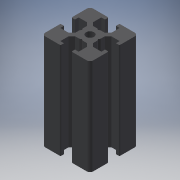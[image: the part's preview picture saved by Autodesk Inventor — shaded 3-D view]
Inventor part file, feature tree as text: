
AUTODESK INVENTOR PART (.ipt)
format: ipt  version: 2016 (Build 200138000, 138)  size: 172,544 bytes
history: native  units: mm
features: extrude x1, sketch x1
ambient origin geometry x8: Origin, YZ Plane, XZ Plane, XY Plane, X Axis, Y Axis, Z Axis, Center Point
bodies: Solid1 (feature_tree)
feature tree (2):
  extrude  "Extrusion1"  [1 undecoded]
  sketch  "Sketch_1"  dims[d0=30.0mm d1=0.0mm]
note: 1 required parameter value undecoded (feature->parameter linkage not recoverable at this tier; creation-order binding heuristic only, values carry confidence <= 0.55)
